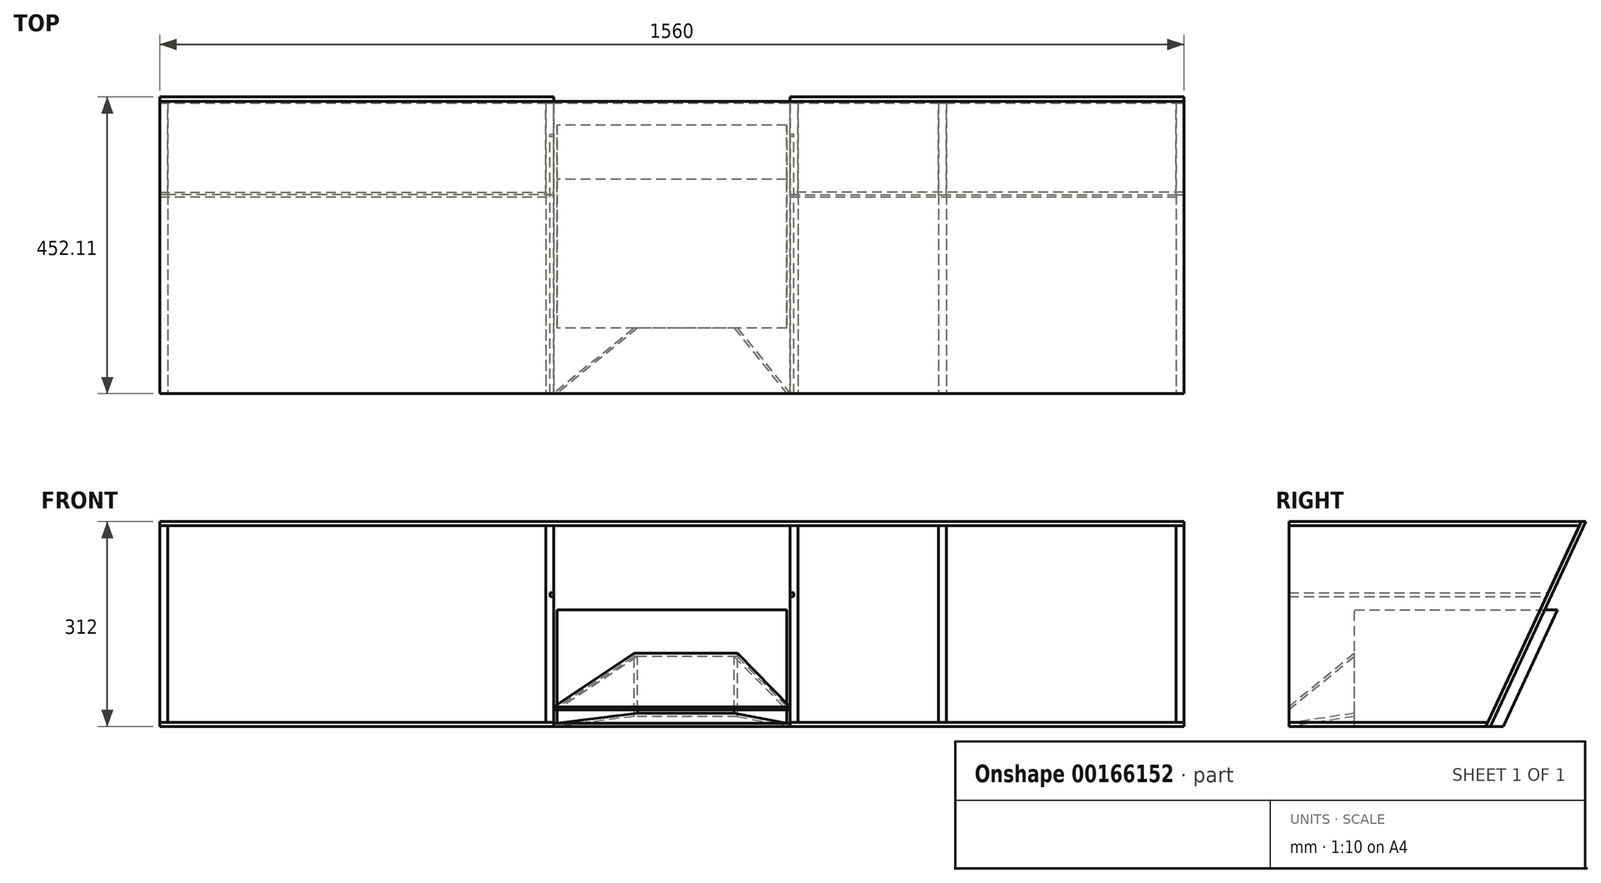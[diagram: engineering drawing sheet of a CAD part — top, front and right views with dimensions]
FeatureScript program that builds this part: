
annotation { "Feature Type Name" : "Feature", "Feature Type Description" : "" }
export const myFeature = defineFeature(function(context is Context, id is Id, definition is map)
    precondition{}
    {
        {
            var Q0;
            Q0=qCreatedBy(makeId("Right.planeOp"),FACE);
            cPlane(context, id + "F0", {"entities" : qUnion([Q0]), "cplaneType" : CPlaneType.OFFSET, "offset" : 480 * mm, "oppositeDirection" : true, "width" : 150 * mm, "height" : 150 * mm});
        }
        {
            var Q0;
            Q0=qCreatedBy(id+"F0.planeOp",FACE);
            var sketch = newSketch(context, id + "F1", { "sketchPlane" : qUnion([Q0])});
            skLineSegment(sketch, "E0", {"start": v(302.8, 6) * mm, "end": v(0, 6) * mm});
            skLineSegment(sketch, "E1", {"start": v(0, 6) * mm, "end": v(0, 0) * mm});
            skLineSegment(sketch, "E2", {"start": v(0, 0) * mm, "end": v(300, 0) * mm});
            skLineSegment(sketch, "E3", {"start": v(300, 0) * mm, "end": v(302.8, 6) * mm});
            skLineSegment(sketch, "E4", {"start": v(0, 6) * mm, "end": v(0, 306) * mm, "construction": true});
            skLineSegment(sketch, "E5", {"start": v(0, 306) * mm, "end": v(442.7, 306) * mm});
            skLineSegment(sketch, "E6", {"start": v(442.7, 306) * mm, "end": v(302.8, 6) * mm});
            skLineSegment(sketch, "E7", {"start": v(0, 306) * mm, "end": v(0, 312) * mm});
            skLineSegment(sketch, "E8", {"start": v(0, 312) * mm, "end": v(445.49, 312) * mm});
            skLineSegment(sketch, "E9", {"start": v(445.49, 312) * mm, "end": v(442.7, 306) * mm});
            skLineSegment(sketch, "E10", {"start": v(452.1, 312) * mm, "end": v(306.62, 0) * mm});
            skLineSegment(sketch, "E11", {"start": v(306.62, 0) * mm, "end": v(300, 0) * mm});
            skLineSegment(sketch, "E12", {"start": v(452.1, 312) * mm, "end": v(445.49, 312) * mm});
            skSolve(sketch);
        }
        {
            var Q0;
            Q0=makeQuery(id+"F1.imprint","IMPRINT",FACE,{"disambiguationData":[TD([[makeQuery(id+"F1.imprint","IMPRINT",EDGE,{"derivedFrom":sQuery(id+"F1.wireOp",EDGE,"E0")}),1.0]])]});
            extrude(context, id + "F2", {"entities" : qUnion([Q0]), "endBound" : BoundingType.SYMMETRIC, "depth" : 600 * mm});
        }
        {
            var Q0;
            Q0=makeQuery(id+"F2.opExtrude","CAP_FACE",FACE,{"disambiguationData":[OSD([sQuery(id+"F1.wireOp",EDGE,"E0"),sQuery(id+"F1.wireOp",EDGE,"E1"),sQuery(id+"F1.wireOp",EDGE,"E2"),sQuery(id+"F1.wireOp",EDGE,"E3")])],"isStart":true});
            var sketch = newSketch(context, id + "F3", { "sketchPlane" : qUnion([Q0])});
            skLineSegment(sketch, "E13", {"start": v(-442.7, 306) * mm, "end": v(0, 306) * mm});
            skLineSegment(sketch, "E14", {"start": v(0, 306) * mm, "end": v(0, 6) * mm});
            skLineSegment(sketch, "E15", {"start": v(-302.8, 6) * mm, "end": v(-442.7, 306) * mm});
            skSolve(sketch);
        }
        {
            var Q0;
            Q0=makeQuery(id+"F3.imprint","IMPRINT",FACE,{"disambiguationData":[TD([[makeQuery(id+"F3.imprint","IMPRINT",EDGE,{"derivedFrom":sQuery(id+"F3.wireOp",EDGE,"E13")}),-1.0]])]});
            extrude(context, id + "F4", {"entities" : qUnion([Q0]), "oppositeDirection" : true, "depth" : 12 * mm});
        }
        {
            var Q0;
            Q0=makeQuery(id+"F4.opExtrude","SWEPT_BODY",BODY,{"disambiguationData":[OSD([sQuery(id+"F1.wireOp",EDGE,"E0"),sQuery(id+"F3.wireOp",EDGE,"E13"),sQuery(id+"F3.wireOp",EDGE,"E14"),sQuery(id+"F3.wireOp",EDGE,"E15")])]});
            var Q1;
            Q1=qCreatedBy(id+"F0.planeOp",FACE);
            mirror(context, id + "F5", {"entities" : qUnion([Q0]), "mirrorPlane" : qUnion([Q1])});
        }
        {
            var Q0;
            Q0=makeQuery(id+"F1.imprint","IMPRINT",FACE,{"disambiguationData":[TD([[makeQuery(id+"F1.imprint","IMPRINT",EDGE,{"derivedFrom":sQuery(id+"F1.wireOp",EDGE,"E3")}),-1.0]])]});
            var Q1;
            Q1=makeQuery(id+"F4.opExtrude","CAP_FACE",FACE,{"disambiguationData":[OSD([sQuery(id+"F1.wireOp",EDGE,"E0"),sQuery(id+"F3.wireOp",EDGE,"E13"),sQuery(id+"F3.wireOp",EDGE,"E14"),sQuery(id+"F3.wireOp",EDGE,"E15")])],"isStart":true});
            var Q2;
            Q2=makeQuery(id+"F5.opPattern","COPY",FACE,{"derivedFrom":makeQuery(id+"F4.opExtrude","CAP_FACE",FACE,{"disambiguationData":[OSD([sQuery(id+"F1.wireOp",EDGE,"E0"),sQuery(id+"F3.wireOp",EDGE,"E13"),sQuery(id+"F3.wireOp",EDGE,"E14"),sQuery(id+"F3.wireOp",EDGE,"E15")])],"isStart":true}),"instanceName":"1"});
            extrude(context, id + "F6", {"entities" : qUnion([Q0]), "endBound" : BoundingType.UP_TO_SURFACE, "oppositeDirection" : true, "endBoundEntityFace" : qUnion([Q1]), "depth" : 25 * mm, "hasSecondDirection" : true, "secondDirectionBound" : SecondDirectionBoundingType.UP_TO_SURFACE, "secondDirectionOppositeDirection" : false, "secondDirectionBoundEntityFace" : qUnion([Q2]), "secondDirectionDepth" : 25 * mm});
        }
        {
            var Q0;
            Q0=qCreatedBy(makeId("Right.planeOp"),FACE);
            var sketch = newSketch(context, id + "F7", { "sketchPlane" : qUnion([Q0])});
            skLineSegment(sketch, "E16", {"start": v(100, 0) * mm, "end": v(100, 177.78) * mm});
            skLineSegment(sketch, "E17", {"start": v(100, 177.78) * mm, "end": v(409.26, 177.78) * mm});
            skLineSegment(sketch, "E18", {"start": v(409.26, 177.78) * mm, "end": v(326.36, 0) * mm});
            skLineSegment(sketch, "E19", {"start": v(326.36, 0) * mm, "end": v(100, 0) * mm});
            skSolve(sketch);
        }
        {
            var Q0;
            Q0=makeQuery(id+"F7.imprint","IMPRINT",FACE,{"disambiguationData":[TD([[makeQuery(id+"F7.imprint","IMPRINT",EDGE,{"derivedFrom":sQuery(id+"F7.wireOp",EDGE,"E16")}),-1.0]])]});
            extrude(context, id + "F8", {"entities" : qUnion([Q0]), "endBound" : BoundingType.SYMMETRIC, "depth" : 350 * mm});
        }
        {
            var Q0;
            Q0=makeQuery(id+"F8.opExtrude","SWEPT_FACE",FACE,{"disambiguationData":[OSD([sQuery(id+"F7.wireOp",EDGE,"E16")])]});
            var sketch = newSketch(context, id + "F9", { "sketchPlane" : qUnion([Q0])});
            skLineSegment(sketch, "E20.bottom", {"start": v(99.86, 20.15) * mm, "end": v(-57.64, 20.15) * mm});
            skLineSegment(sketch, "E20.top", {"start": v(99.86, 106.62) * mm, "end": v(-57.64, 106.62) * mm});
            skLineSegment(sketch, "E20.left", {"start": v(94.86, 20.15) * mm, "end": v(94.86, 106.62) * mm});
            skLineSegment(sketch, "E20.right", {"start": v(-52.64, 20.15) * mm, "end": v(-52.64, 106.62) * mm});
            skPoint(sketch, "E20.middle", {"position": v(21.11, 63.39) * mm});
            skLineSegment(sketch, "E21.0", {"start": v(99.86, 111.62) * mm, "end": v(-57.64, 111.62) * mm});
            skLineSegment(sketch, "E21.1", {"start": v(99.86, 15.15) * mm, "end": v(99.86, 111.62) * mm});
            skLineSegment(sketch, "E21.2", {"start": v(99.86, 15.15) * mm, "end": v(-57.64, 15.15) * mm});
            skLineSegment(sketch, "E21.3", {"start": v(-57.64, 15.15) * mm, "end": v(-57.64, 111.62) * mm});
            skSolve(sketch);
        }
        {
            var Q0;
            Q0=qCreatedBy(makeId("Front.planeOp"),FACE);
            var sketch = newSketch(context, id + "F10", { "sketchPlane" : qUnion([Q0])});
            skLineSegment(sketch, "E22.bottom", {"start": v(-180, 0) * mm, "end": v(180, 0) * mm});
            skLineSegment(sketch, "E22.top", {"start": v(-180, 30) * mm, "end": v(180, 30) * mm});
            skLineSegment(sketch, "E22.left", {"start": v(-180, 0) * mm, "end": v(-180, 30) * mm});
            skLineSegment(sketch, "E22.right", {"start": v(180, 0) * mm, "end": v(180, 30) * mm});
            skLineSegment(sketch, "E23.0", {"start": v(-180, 25) * mm, "end": v(180, 25) * mm});
            skLineSegment(sketch, "E23.1", {"start": v(-175, 5) * mm, "end": v(-175, 25) * mm});
            skLineSegment(sketch, "E23.2", {"start": v(-180, 5) * mm, "end": v(180, 5) * mm});
            skLineSegment(sketch, "E23.3", {"start": v(175, 5) * mm, "end": v(175, 25) * mm});
            skSolve(sketch);
        }
        {
            var Q1;
            {var subQ0=sQuery(id+"F9.wireOp",EDGE,"E21.0");Q1=makeQuery(id+"F9.imprint","IMPRINT",FACE,{"disambiguationData":[TD([[makeQuery(id+"F9.imprint","IMPRINT",EDGE,{"derivedFrom":subQ0}),1.0]])]});}
            var Q2;
            {var subQ4=sQuery(id+"F10.wireOp",EDGE,"E22.top");Q2=makeQuery(id+"F10.imprint","IMPRINT",FACE,{"disambiguationData":[TD([[makeQuery(id+"F10.imprint","IMPRINT",EDGE,{"derivedFrom":subQ4}),-1.0]])]});}
            loft(context, id + "F11", {"sheetProfilesArray" : [{ "sheetProfileEntities" : qUnion([Q1]) }, { "sheetProfileEntities" : qUnion([Q2]) }]});
        }
        {
            var Q1;
            {var subQ3=sQuery(id+"F9.wireOp",EDGE,"E21.2");Q1=makeQuery(id+"F9.imprint","IMPRINT",FACE,{"disambiguationData":[TD([[makeQuery(id+"F9.imprint","IMPRINT",EDGE,{"derivedFrom":subQ3}),-1.0]])]});}
            var Q2;
            {var subQ5=sQuery(id+"F10.wireOp",EDGE,"E22.bottom");Q2=makeQuery(id+"F10.imprint","IMPRINT",FACE,{"disambiguationData":[TD([[makeQuery(id+"F10.imprint","IMPRINT",EDGE,{"derivedFrom":subQ5}),1.0]])]});}
            loft(context, id + "F12", {"sheetProfilesArray" : [{ "sheetProfileEntities" : qUnion([Q1]) }, { "sheetProfileEntities" : qUnion([Q2]) }]});
        }
        {
            var Q0;
            {var subQ3=sQuery(id+"F9.wireOp",EDGE,"E20.left");Q0=makeQuery(id+"F9.imprint","IMPRINT",FACE,{"disambiguationData":[TD([[makeQuery(id+"F9.imprint","IMPRINT",EDGE,{"derivedFrom":subQ3}),-1.0]])]});}
            var Q1;
            {var subQ5=sQuery(id+"F10.wireOp",EDGE,"E23.3");Q1=makeQuery(id+"F10.imprint","IMPRINT",FACE,{"disambiguationData":[TD([[makeQuery(id+"F10.imprint","IMPRINT",EDGE,{"derivedFrom":subQ5}),-1.0]])]});}
            loft(context, id + "F13", {"sheetProfilesArray" : [{ "sheetProfileEntities" : qUnion([Q0]) }, { "sheetProfileEntities" : qUnion([Q1]) }]});
        }
        {
            var Q0;
            {var subQ3=sQuery(id+"F9.wireOp",EDGE,"E20.right");Q0=makeQuery(id+"F9.imprint","IMPRINT",FACE,{"disambiguationData":[TD([[makeQuery(id+"F9.imprint","IMPRINT",EDGE,{"derivedFrom":subQ3}),1.0]])]});}
            var Q1;
            {var subQ5=sQuery(id+"F10.wireOp",EDGE,"E23.1");Q1=makeQuery(id+"F10.imprint","IMPRINT",FACE,{"disambiguationData":[TD([[makeQuery(id+"F10.imprint","IMPRINT",EDGE,{"derivedFrom":subQ5}),1.0]])]});}
            loft(context, id + "F14", {"sheetProfilesArray" : [{ "sheetProfileEntities" : qUnion([Q0]) }, { "sheetProfileEntities" : qUnion([Q1]) }]});
        }
        {
            var Q0;
            Q0=makeQuery(id+"F5.opPattern","COPY",FACE,{"derivedFrom":makeQuery(id+"F4.opExtrude","CAP_FACE",FACE,{"disambiguationData":[OSD([sQuery(id+"F1.wireOp",EDGE,"E0"),sQuery(id+"F3.wireOp",EDGE,"E13"),sQuery(id+"F3.wireOp",EDGE,"E14"),sQuery(id+"F3.wireOp",EDGE,"E15")])],"isStart":true}),"instanceName":"1"});
            var sketch = newSketch(context, id + "F15", { "sketchPlane" : qUnion([Q0])});
            skLineSegment(sketch, "E24.bottom", {"start": v(0, 197.78) * mm, "end": v(395.03, 197.78) * mm});
            skLineSegment(sketch, "E24.top", {"start": v(0, 203.78) * mm, "end": v(395.03, 203.78) * mm});
            skLineSegment(sketch, "E24.left", {"start": v(0, 197.78) * mm, "end": v(0, 203.78) * mm});
            skLineSegment(sketch, "E24.right", {"start": v(395.03, 197.78) * mm, "end": v(395.03, 203.78) * mm});
            skSolve(sketch);
        }
        {
            var Q0;
            {var subQ4=sQuery(id+"F15.wireOp",EDGE,"E24.top");Q0=makeQuery(id+"F15.imprint","IMPRINT",FACE,{"disambiguationData":[TD([[makeQuery(id+"F15.imprint","IMPRINT",EDGE,{"derivedFrom":subQ4}),-1.0]])]});}
            extrude(context, id + "F16", {"entities" : qUnion([Q0]), "operationType" : NewBodyOperationType.REMOVE, "oppositeDirection" : true, "depth" : 6 * mm});
        }
        {
            var Q0;
            Q0=makeQuery(id+"F5.opPattern","COPY",BODY,{"derivedFrom":makeQuery(id+"F4.opExtrude","SWEPT_BODY",BODY,{"disambiguationData":[OSD([sQuery(id+"F1.wireOp",EDGE,"E0"),sQuery(id+"F3.wireOp",EDGE,"E13"),sQuery(id+"F3.wireOp",EDGE,"E14"),sQuery(id+"F3.wireOp",EDGE,"E15")])]}),"instanceName":"1"});
            var Q1;
            Q1=makeQuery(id+"F6.opExtrude","SWEPT_BODY",BODY,{"disambiguationData":[OSD([sQuery(id+"F1.wireOp",EDGE,"E3"),sQuery(id+"F1.wireOp",EDGE,"E6"),sQuery(id+"F1.wireOp",EDGE,"E9"),sQuery(id+"F1.wireOp",EDGE,"E10"),sQuery(id+"F1.wireOp",EDGE,"E11"),sQuery(id+"F1.wireOp",EDGE,"E12")])]});
            var Q2;
            Q2=makeQuery(id+"F4.opExtrude","SWEPT_BODY",BODY,{"disambiguationData":[OSD([sQuery(id+"F1.wireOp",EDGE,"E0"),sQuery(id+"F3.wireOp",EDGE,"E13"),sQuery(id+"F3.wireOp",EDGE,"E14"),sQuery(id+"F3.wireOp",EDGE,"E15")])]});
            var Q3;
            Q3=makeQuery(id+"F2.opExtrude","SWEPT_BODY",BODY,{"disambiguationData":[OSD([sQuery(id+"F1.wireOp",EDGE,"E0"),sQuery(id+"F1.wireOp",EDGE,"E1"),sQuery(id+"F1.wireOp",EDGE,"E2"),sQuery(id+"F1.wireOp",EDGE,"E3")])]});
            var Q4;
            Q4=qCreatedBy(makeId("Right.planeOp"),FACE);
            mirror(context, id + "F17", {"entities" : qUnion([Q0, Q1, Q2, Q3]), "mirrorPlane" : qUnion([Q4])});
        }
        {
            var Q0;
            Q0=makeQuery(id+"F17.opPattern","COPY",BODY,{"derivedFrom":makeQuery(id+"F4.opExtrude","SWEPT_BODY",BODY,{"disambiguationData":[OSD([sQuery(id+"F1.wireOp",EDGE,"E0"),sQuery(id+"F3.wireOp",EDGE,"E13"),sQuery(id+"F3.wireOp",EDGE,"E14"),sQuery(id+"F3.wireOp",EDGE,"E15")])]}),"instanceName":"1"});
            transform(context, id + "F18", {"entities" : qUnion([Q0]), "transformType" : TransformType.TRANSLATION_3D, "dx" : -362 * mm, "dy" : 0 * mm, "dz" : 0 * mm, "makeCopy" : true});
        }
        {
            var Q0;
            Q0=makeQuery(id+"F1.imprint","IMPRINT",FACE,{"disambiguationData":[TD([[makeQuery(id+"F1.imprint","IMPRINT",EDGE,{"derivedFrom":sQuery(id+"F1.wireOp",EDGE,"E5")}),1.0]])]});
            var Q1;
            Q1=makeQuery(id+"F4.opExtrude","CAP_FACE",FACE,{"disambiguationData":[OSD([sQuery(id+"F1.wireOp",EDGE,"E0"),sQuery(id+"F3.wireOp",EDGE,"E13"),sQuery(id+"F3.wireOp",EDGE,"E14"),sQuery(id+"F3.wireOp",EDGE,"E15")])],"isStart":true});
            var Q2;
            Q2=makeQuery(id+"F17.opPattern","COPY",FACE,{"derivedFrom":makeQuery(id+"F4.opExtrude","CAP_FACE",FACE,{"disambiguationData":[OSD([sQuery(id+"F1.wireOp",EDGE,"E0"),sQuery(id+"F3.wireOp",EDGE,"E13"),sQuery(id+"F3.wireOp",EDGE,"E14"),sQuery(id+"F3.wireOp",EDGE,"E15")])],"isStart":true}),"instanceName":"1"});
            extrude(context, id + "F19", {"entities" : qUnion([Q0]), "endBound" : BoundingType.UP_TO_SURFACE, "oppositeDirection" : true, "endBoundEntityFace" : qUnion([Q1]), "depth" : 25 * mm, "hasSecondDirection" : true, "secondDirectionBound" : SecondDirectionBoundingType.UP_TO_SURFACE, "secondDirectionOppositeDirection" : false, "secondDirectionBoundEntityFace" : qUnion([Q2]), "secondDirectionDepth" : 25 * mm});
        }
    });
